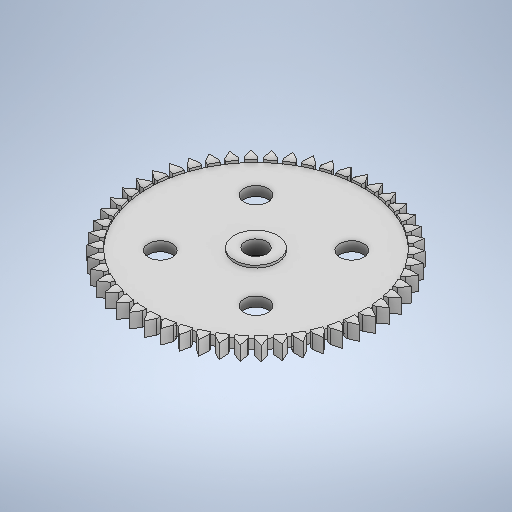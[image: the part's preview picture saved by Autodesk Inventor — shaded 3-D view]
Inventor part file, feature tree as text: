
AUTODESK INVENTOR PART (.ipt)
format: ipt  version: 2025.2 (Build 292293000, 293)  size: 571,392 bytes
history: native  units: mm
features: extrude x3, sketch x3, pattern_circular x1
ambient origin geometry x8: Origin, YZ Plane, XZ Plane, XY Plane, X Axis, Y Axis, Z Axis, Center Point
bodies: Solid1 (feature_tree)
feature tree (7):
  extrude  "Extrusion1"  Depth=45.0mm
  extrude  "Extrusion2"  Depth=4.5mm
  pattern_circular  "Circular Pattern1"  Count=2  [1 undecoded]
  extrude  "Extrusion3"  Depth=2.5mm
  sketch  "Sketch1"  dims[d0=50.0mm d1=45.0mm]
  sketch  "Sketch2"  dims[d2=4.5mm d3=20.0mm d4=20.0mm]
  sketch  "Sketch3"  dims[d5=5.0mm d6=5.0mm d7=5.0mm d8=5.0mm d9=2.0mm d10=0.0mm d11=50.0mm d12=2.0mm d13=30.0deg d14=2.0mm d15=0.5mm d16=2.5mm d17=0.0mm d18=0.0mm d19=500.0mm d20=360.0deg d22=9.0mm d23=0.5mm d24=2.5mm d25=0.0mm d26=0.0mm]
note: 1 required parameter value undecoded (feature->parameter linkage not recoverable at this tier; creation-order binding heuristic only, values carry confidence <= 0.55)
